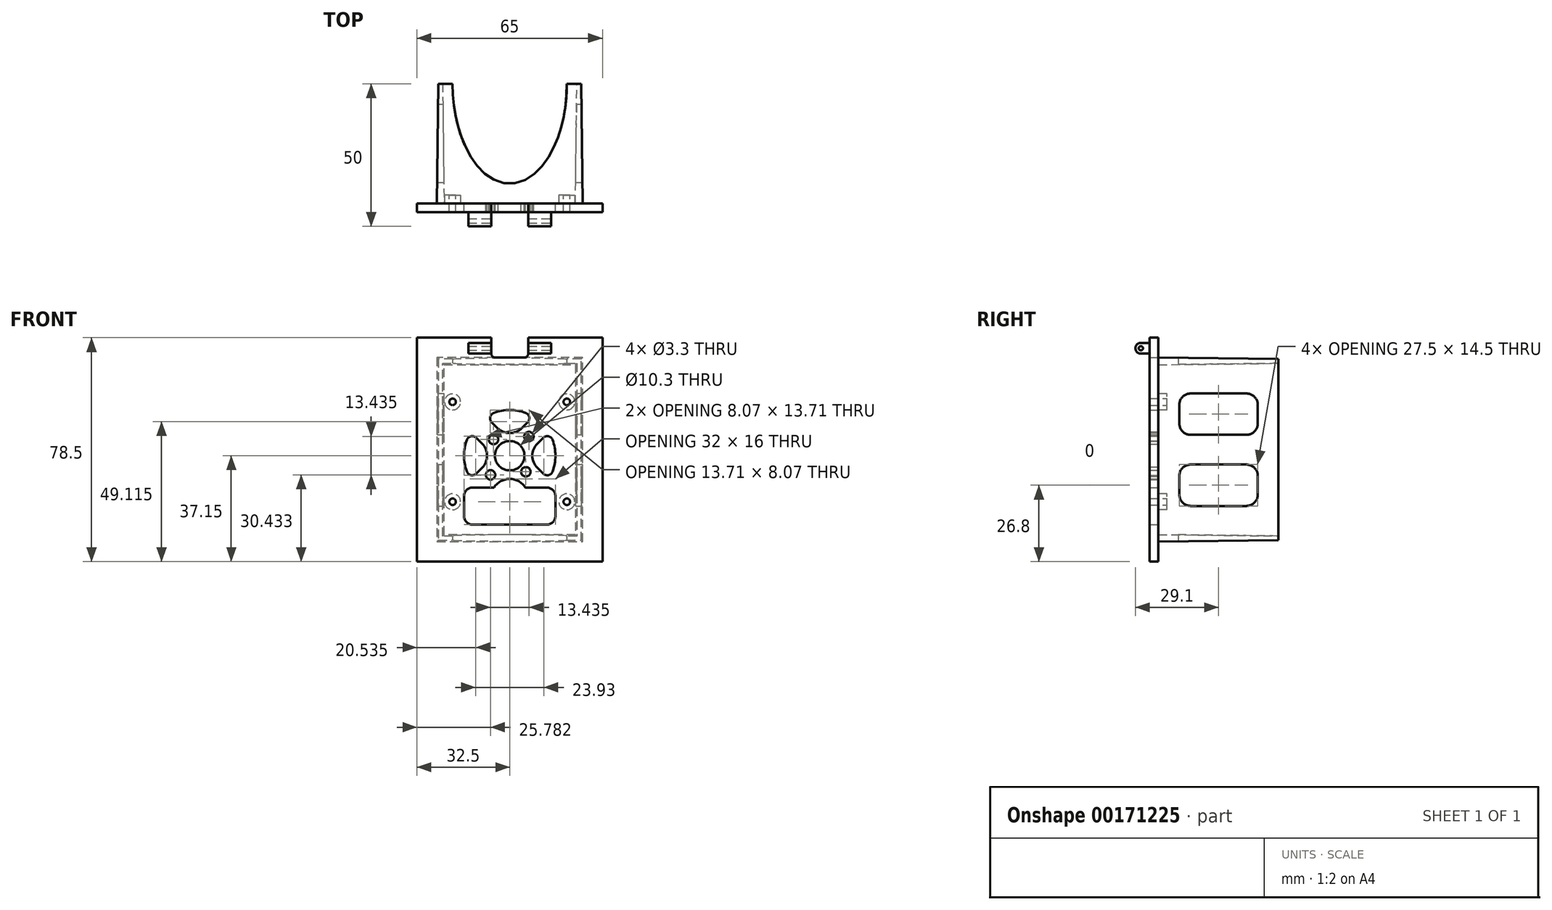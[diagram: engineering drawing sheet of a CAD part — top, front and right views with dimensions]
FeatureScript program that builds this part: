
annotation { "Feature Type Name" : "Feature", "Feature Type Description" : "" }
export const myFeature = defineFeature(function(context is Context, id is Id, definition is map)
    precondition{}
    {
        {
            var Q0;
            Q0=qCreatedBy(makeId("Front.planeOp"),FACE);
            var sketch = newSketch(context, id + "F0", { "sketchPlane" : qUnion([Q0])});
            skLineSegment(sketch, "E0.bottom", {"start": v(-32.5, 0) * mm, "end": v(32.5, 0) * mm});
            skLineSegment(sketch, "E0.top", {"start": v(-32.5, 78.5) * mm, "end": v(32.5, 78.5) * mm});
            skLineSegment(sketch, "E0.left", {"start": v(-32.5, 0) * mm, "end": v(-32.5, 78.5) * mm});
            skLineSegment(sketch, "E0.right", {"start": v(32.5, 0) * mm, "end": v(32.5, 78.5) * mm});
            skLineSegment(sketch, "E1", {"start": v(0, 0) * mm, "end": v(0, 78.5) * mm, "construction": true});
            skLineSegment(sketch, "E2", {"start": v(-6.5, 78.5) * mm, "end": v(-6.5, 73) * mm});
            skLineSegment(sketch, "E3", {"start": v(-5, 71.5) * mm, "end": v(0, 71.5) * mm});
            skLineSegment(sketch, "E4.MirrorCS", {"start": v(5, 71.5) * mm, "end": v(0, 71.5) * mm});
            skLineSegment(sketch, "E5.MirrorCS", {"start": v(6.5, 78.5) * mm, "end": v(6.5, 73) * mm});
            skPoint(sketch, "E6.visualSharp", {"position": v(-6.5, 71.5) * mm});
            skArc(sketch, "E6.filletArc", {"start": v(-6.5, 73) * mm, "mid": v(-6.06, 71.94) * mm, "end": v(-5, 71.5) * mm});
            skPoint(sketch, "E7.visualSharp", {"position": v(6.5, 71.5) * mm});
            skArc(sketch, "E7.filletArc", {"start": v(5, 71.5) * mm, "mid": v(6.06, 71.94) * mm, "end": v(6.5, 73) * mm});
            skCircle(sketch, "E8", {"center": v(0, 37.15) * mm, "radius": 5.15 * mm});
            skLineSegment(sketch, "E9.bottom", {"start": v(-13, 26) * mm, "end": v(-5.5, 26) * mm});
            skLineSegment(sketch, "E9.top", {"start": v(-13, 13) * mm, "end": v(13, 13) * mm});
            skLineSegment(sketch, "E9.left", {"start": v(-16, 23) * mm, "end": v(-16, 16) * mm});
            skLineSegment(sketch, "E9.right", {"start": v(16, 23) * mm, "end": v(16, 16) * mm});
            skPoint(sketch, "E9.middle", {"position": v(0, 19.5) * mm});
            skArc(sketch, "E10", {"start": v(5.5, 26) * mm, "mid": v(0, 29) * mm, "end": v(-5.5, 26) * mm});
            skLineSegment(sketch, "E11.trimOffspring", {"start": v(5.5, 26) * mm, "end": v(13, 26) * mm});
            skPoint(sketch, "E12.visualSharp", {"position": v(-16, 26) * mm});
            skArc(sketch, "E12.filletArc", {"start": v(-13, 26) * mm, "mid": v(-15.12, 25.12) * mm, "end": v(-16, 23) * mm});
            skPoint(sketch, "E13.visualSharp", {"position": v(-16, 13) * mm});
            skArc(sketch, "E13.filletArc", {"start": v(-16, 16) * mm, "mid": v(-15.12, 13.88) * mm, "end": v(-13, 13) * mm});
            skPoint(sketch, "E14.visualSharp", {"position": v(16, 13) * mm});
            skArc(sketch, "E14.filletArc", {"start": v(13, 13) * mm, "mid": v(15.12, 13.88) * mm, "end": v(16, 16) * mm});
            skPoint(sketch, "E15.visualSharp", {"position": v(16, 26) * mm});
            skArc(sketch, "E15.filletArc", {"start": v(16, 23) * mm, "mid": v(15.12, 25.12) * mm, "end": v(13, 26) * mm});
            skCircle(sketch, "E16", {"center": v(-20, 56) * mm, "radius": 1.15 * mm});
            skCircle(sketch, "E17", {"center": v(-20, 21) * mm, "radius": 1.15 * mm});
            skCircle(sketch, "E18.MirrorC", {"center": v(20, 56) * mm, "radius": 1.15 * mm});
            skCircle(sketch, "E19.MirrorC", {"center": v(20, 21) * mm, "radius": 1.15 * mm});
            skLineSegment(sketch, "E20", {"start": v(0, 37.15) * mm, "end": v(-11.31, 48.46) * mm, "construction": true});
            skLineSegment(sketch, "E21.1.0", {"start": v(0, 37.15) * mm, "end": v(-11.31, 25.84) * mm, "construction": true});
            skLineSegment(sketch, "E21.2.0", {"start": v(0, 37.15) * mm, "end": v(11.31, 25.84) * mm, "construction": true});
            skLineSegment(sketch, "E21.3.0", {"start": v(0, 37.15) * mm, "end": v(11.31, 48.46) * mm, "construction": true});
            skLineSegment(sketch, "E22", {"start": v(-4.24, 46.84) * mm, "end": v(-6.27, 48.87) * mm});
            skLineSegment(sketch, "E23.MirrorCS", {"start": v(4.24, 46.84) * mm, "end": v(6.27, 48.87) * mm});
            skArc(sketch, "E24", {"start": v(5.55, 52.16) * mm, "mid": v(0, 53.15) * mm, "end": v(-5.55, 52.16) * mm});
            skArc(sketch, "E25", {"start": v(-4.24, 46.84) * mm, "mid": v(0, 45.08) * mm, "end": v(4.24, 46.84) * mm});
            skPoint(sketch, "E26.orphan", {"position": v(2.24, 44.83) * mm});
            skPoint(sketch, "E27.orphan", {"position": v(-2.24, 44.83) * mm});
            skPoint(sketch, "E28.visualSharp", {"position": v(-8.26, 50.85) * mm});
            skArc(sketch, "E28.filletArc", {"start": v(-5.55, 52.16) * mm, "mid": v(-6.81, 50.7) * mm, "end": v(-6.27, 48.87) * mm});
            skPoint(sketch, "E29.visualSharp", {"position": v(8.26, 50.85) * mm});
            skArc(sketch, "E29.filletArc", {"start": v(6.27, 48.87) * mm, "mid": v(6.81, 50.7) * mm, "end": v(5.55, 52.16) * mm});
            skArc(sketch, "E30.MirrorCS", {"start": v(15, 42.7) * mm, "mid": v(16, 37.15) * mm, "end": v(15, 31.6) * mm});
            skArc(sketch, "E31.MirrorCS", {"start": v(11.72, 43.42) * mm, "mid": v(13.56, 43.96) * mm, "end": v(15, 42.7) * mm});
            skLineSegment(sketch, "E32.MirrorCS", {"start": v(9.69, 41.4) * mm, "end": v(11.72, 43.42) * mm});
            skArc(sketch, "E33.MirrorCS", {"start": v(9.69, 32.9) * mm, "mid": v(7.93, 37.15) * mm, "end": v(9.69, 41.4) * mm});
            skLineSegment(sketch, "E34.MirrorCS", {"start": v(9.69, 32.9) * mm, "end": v(11.72, 30.88) * mm});
            skArc(sketch, "E35.MirrorCS", {"start": v(15, 31.6) * mm, "mid": v(13.56, 30.34) * mm, "end": v(11.72, 30.88) * mm});
            skArc(sketch, "E36.MirrorCS", {"start": v(-15, 31.6) * mm, "mid": v(-16, 37.15) * mm, "end": v(-15, 42.7) * mm});
            skArc(sketch, "E37.MirrorCS", {"start": v(-11.72, 30.88) * mm, "mid": v(-13.56, 30.34) * mm, "end": v(-15, 31.6) * mm});
            skLineSegment(sketch, "E38.MirrorCS", {"start": v(-9.69, 32.9) * mm, "end": v(-11.72, 30.88) * mm});
            skArc(sketch, "E39.MirrorCS", {"start": v(-9.69, 41.4) * mm, "mid": v(-7.93, 37.15) * mm, "end": v(-9.69, 32.9) * mm});
            skLineSegment(sketch, "E40.MirrorCS", {"start": v(-9.69, 41.4) * mm, "end": v(-11.72, 43.42) * mm});
            skArc(sketch, "E41.MirrorCS", {"start": v(-15, 42.7) * mm, "mid": v(-13.56, 43.96) * mm, "end": v(-11.72, 43.42) * mm});
            skCircle(sketch, "E42", {"center": v(-5.66, 42.8) * mm, "radius": 1.65 * mm});
            skCircle(sketch, "E43.MirrorC", {"center": v(5.66, 31.5) * mm, "radius": 1.65 * mm});
            skCircle(sketch, "E44", {"center": v(-6.72, 30.43) * mm, "radius": 1.65 * mm});
            skCircle(sketch, "E45.MirrorC", {"center": v(6.72, 43.87) * mm, "radius": 1.65 * mm});
            skSolve(sketch);
        }
        {
            var Q0;
            Q0=makeQuery(id+"F0.imprint","IMPRINT",FACE,{"disambiguationData":[TD([[makeQuery(id+"F0.imprint","IMPRINT",EDGE,{"derivedFrom":sQuery(id+"F0.wireOp",EDGE,"E0.bottom")}),1.0]])]});
            extrude(context, id + "F1", {"entities" : qUnion([Q0]), "depth" : 3 * mm});
        }
        {
            var Q0;
            Q0=makeQuery(id+"F1.opExtrude","CAP_FACE",FACE,{"disambiguationData":[OSD([sQuery(id+"F0.wireOp",EDGE,"E0.bottom"),sQuery(id+"F0.wireOp",EDGE,"E0.top"),sQuery(id+"F0.wireOp",EDGE,"E0.left"),sQuery(id+"F0.wireOp",EDGE,"E0.right"),sQuery(id+"F0.wireOp",EDGE,"E2"),sQuery(id+"F0.wireOp",EDGE,"E3"),sQuery(id+"F0.wireOp",EDGE,"E4.MirrorCS"),sQuery(id+"F0.wireOp",EDGE,"E5.MirrorCS"),sQuery(id+"F0.wireOp",EDGE,"E6.filletArc"),sQuery(id+"F0.wireOp",EDGE,"E7.filletArc"),sQuery(id+"F0.wireOp",EDGE,"E8"),sQuery(id+"F0.wireOp",EDGE,"E9.bottom"),sQuery(id+"F0.wireOp",EDGE,"E9.top"),sQuery(id+"F0.wireOp",EDGE,"E9.left"),sQuery(id+"F0.wireOp",EDGE,"E9.right"),sQuery(id+"F0.wireOp",EDGE,"E10"),sQuery(id+"F0.wireOp",EDGE,"E11.trimOffspring"),sQuery(id+"F0.wireOp",EDGE,"E12.filletArc"),sQuery(id+"F0.wireOp",EDGE,"E13.filletArc"),sQuery(id+"F0.wireOp",EDGE,"E14.filletArc"),sQuery(id+"F0.wireOp",EDGE,"E15.filletArc"),sQuery(id+"F0.wireOp",EDGE,"E16"),sQuery(id+"F0.wireOp",EDGE,"E17"),sQuery(id+"F0.wireOp",EDGE,"E18.MirrorC"),sQuery(id+"F0.wireOp",EDGE,"E19.MirrorC"),sQuery(id+"F0.wireOp",EDGE,"E22"),sQuery(id+"F0.wireOp",EDGE,"E23.MirrorCS"),sQuery(id+"F0.wireOp",EDGE,"E24"),sQuery(id+"F0.wireOp",EDGE,"E25"),sQuery(id+"F0.wireOp",EDGE,"E28.filletArc"),sQuery(id+"F0.wireOp",EDGE,"E29.filletArc"),sQuery(id+"F0.wireOp",EDGE,"E30.MirrorCS"),sQuery(id+"F0.wireOp",EDGE,"E31.MirrorCS"),sQuery(id+"F0.wireOp",EDGE,"E32.MirrorCS"),sQuery(id+"F0.wireOp",EDGE,"E33.MirrorCS"),sQuery(id+"F0.wireOp",EDGE,"E34.MirrorCS"),sQuery(id+"F0.wireOp",EDGE,"E35.MirrorCS"),sQuery(id+"F0.wireOp",EDGE,"E36.MirrorCS"),sQuery(id+"F0.wireOp",EDGE,"E37.MirrorCS"),sQuery(id+"F0.wireOp",EDGE,"E38.MirrorCS"),sQuery(id+"F0.wireOp",EDGE,"E39.MirrorCS"),sQuery(id+"F0.wireOp",EDGE,"E40.MirrorCS"),sQuery(id+"F0.wireOp",EDGE,"E41.MirrorCS"),sQuery(id+"F0.wireOp",EDGE,"E42"),sQuery(id+"F0.wireOp",EDGE,"E43.MirrorC"),sQuery(id+"F0.wireOp",EDGE,"E44"),sQuery(id+"F0.wireOp",EDGE,"E45.MirrorC")])],"isStart":true});
            var sketch = newSketch(context, id + "F2", { "sketchPlane" : qUnion([Q0])});
            skLineSegment(sketch, "E46.bottom", {"start": v(-25.5, 71.5) * mm, "end": v(25.5, 71.5) * mm});
            skLineSegment(sketch, "E46.top", {"start": v(-25.5, 7) * mm, "end": v(25.5, 7) * mm});
            skLineSegment(sketch, "E46.left", {"start": v(-25.5, 71.5) * mm, "end": v(-25.5, 7) * mm});
            skLineSegment(sketch, "E46.right", {"start": v(25.5, 71.5) * mm, "end": v(25.5, 7) * mm});
            skLineSegment(sketch, "E47.0", {"start": v(-23, 69) * mm, "end": v(23, 69) * mm});
            skLineSegment(sketch, "E47.1", {"start": v(-23, 69) * mm, "end": v(-23, 9.5) * mm});
            skLineSegment(sketch, "E47.2", {"start": v(-23, 9.5) * mm, "end": v(23, 9.5) * mm});
            skLineSegment(sketch, "E47.3", {"start": v(23, 69) * mm, "end": v(23, 9.5) * mm});
            skLineSegment(sketch, "E48.0", {"start": v(-37.5, -5) * mm, "end": v(37.5, -5) * mm});
            skLineSegment(sketch, "E48.1", {"start": v(-37.5, 83.5) * mm, "end": v(-37.5, -5) * mm});
            skLineSegment(sketch, "E48.2", {"start": v(37.5, -5) * mm, "end": v(37.5, 83.5) * mm});
            skLineSegment(sketch, "E48.3", {"start": v(-1.5, 83.5) * mm, "end": v(-37.5, 83.5) * mm});
            skLineSegment(sketch, "E48.4", {"start": v(37.5, 83.5) * mm, "end": v(1.5, 83.5) * mm});
            skLineSegment(sketch, "E48.5", {"start": v(1.5, 83.5) * mm, "end": v(1.5, 76.5) * mm});
            skLineSegment(sketch, "E48.6", {"start": v(1.5, 76.5) * mm, "end": v(-1.5, 76.5) * mm});
            skLineSegment(sketch, "E48.7", {"start": v(-1.5, 76.5) * mm, "end": v(-1.5, 83.5) * mm});
            skCircle(sketch, "E49", {"center": v(-20, 56) * mm, "radius": 2.8 * mm});
            skCircle(sketch, "E50", {"center": v(20, 56) * mm, "radius": 2.8 * mm});
            skCircle(sketch, "E51", {"center": v(20, 21) * mm, "radius": 2.8 * mm});
            skCircle(sketch, "E52", {"center": v(-20, 21) * mm, "radius": 2.8 * mm});
            skSolve(sketch);
        }
        {
            var Q0;
            Q0=makeQuery(id+"F2.imprint","IMPRINT",FACE,{"disambiguationData":[TD([[makeQuery(id+"F2.imprint","IMPRINT",EDGE,{"derivedFrom":sQuery(id+"F2.wireOp",EDGE,"E46.top")}),1.0]])]});
            extrude(context, id + "F3", {"entities" : qUnion([Q0]), "operationType" : NewBodyOperationType.ADD, "depth" : 42 * mm, "hasDraft" : true, "draftAngle" : .67 * degree, "draftPullDirection" : true});
        }
        {
            var Q0;
            Q0=makeQuery(id+"F2.imprint","IMPRINT",FACE,{"disambiguationData":[TD([[makeQuery(id+"F2.imprint","IMPRINT",EDGE,{"derivedFrom":sQuery(id+"F2.wireOp",EDGE,"E49")}),1.0]])]});
            var Q1;
            Q1=makeQuery(id+"F2.imprint","IMPRINT",FACE,{"disambiguationData":[TD([[makeQuery(id+"F2.imprint","IMPRINT",EDGE,{"derivedFrom":sQuery(id+"F2.wireOp",EDGE,"E50")}),1.0]])]});
            var Q2;
            Q2=makeQuery(id+"F2.imprint","IMPRINT",FACE,{"disambiguationData":[TD([[makeQuery(id+"F2.imprint","IMPRINT",EDGE,{"derivedFrom":sQuery(id+"F2.wireOp",EDGE,"E51")}),1.0]])]});
            var Q3;
            Q3=makeQuery(id+"F2.imprint","IMPRINT",FACE,{"disambiguationData":[TD([[makeQuery(id+"F2.imprint","IMPRINT",EDGE,{"derivedFrom":sQuery(id+"F2.wireOp",EDGE,"E52")}),1.0]])]});
            extrude(context, id + "F4", {"entities" : qUnion([Q0, Q1, Q2, Q3]), "operationType" : NewBodyOperationType.ADD, "depth" : 3 * mm});
        }
        {
            var Q0;
            Q0=qCreatedBy(makeId("Top.planeOp"),FACE);
            var sketch = newSketch(context, id + "F5", { "sketchPlane" : qUnion([Q0])});
            skEllipse(sketch, "E53", {"center": v(0, 42) * mm, "majorRadius": 20 * mm, "minorRadius": 35 * mm, "majorAxis": v(1, 0)});
            skSolve(sketch);
        }
        {
            var Q0;
            Q0=makeQuery(id+"F5.imprint","IMPRINT",FACE,{"disambiguationData":[TD([[makeQuery(id+"F5.imprint","IMPRINT",EDGE,{"derivedFrom":sQuery(id+"F5.wireOp",EDGE,"E53")}),1.0]])]});
            var Q1;
            Q1=makeQuery(id+"F3.opExtrude","SWEPT_FACE",FACE,{"disambiguationData":[OSD([sQuery(id+"F2.wireOp",EDGE,"E46.bottom")])]});
            extrude(context, id + "F6", {"entities" : qUnion([Q0]), "operationType" : NewBodyOperationType.REMOVE, "endBound" : BoundingType.UP_TO_SURFACE, "endBoundEntityFace" : qUnion([Q1]), "depth" : 25 * mm});
        }
        {
            var Q0;
            Q0=qCreatedBy(makeId("Right.planeOp"),FACE);
            var sketch = newSketch(context, id + "F7", { "sketchPlane" : qUnion([Q0])});
            skLineSegment(sketch, "E54.bottom", {"start": v(30.85, 58.95) * mm, "end": v(11.35, 58.95) * mm});
            skLineSegment(sketch, "E54.top", {"start": v(30.85, 44.45) * mm, "end": v(11.35, 44.45) * mm});
            skLineSegment(sketch, "E54.left", {"start": v(34.85, 54.95) * mm, "end": v(34.85, 48.45) * mm});
            skLineSegment(sketch, "E54.right", {"start": v(7.35, 54.95) * mm, "end": v(7.35, 48.45) * mm});
            skPoint(sketch, "E55.visualSharp", {"position": v(34.85, 58.95) * mm});
            skArc(sketch, "E55.filletArc", {"start": v(34.85, 54.95) * mm, "mid": v(33.68, 57.78) * mm, "end": v(30.85, 58.95) * mm});
            skPoint(sketch, "E56.visualSharp", {"position": v(7.35, 58.95) * mm});
            skArc(sketch, "E56.filletArc", {"start": v(11.35, 58.95) * mm, "mid": v(8.52, 57.78) * mm, "end": v(7.35, 54.95) * mm});
            skPoint(sketch, "E57.visualSharp", {"position": v(7.35, 44.45) * mm});
            skArc(sketch, "E57.filletArc", {"start": v(7.35, 48.45) * mm, "mid": v(8.52, 45.62) * mm, "end": v(11.35, 44.45) * mm});
            skPoint(sketch, "E58.visualSharp", {"position": v(34.85, 44.45) * mm});
            skArc(sketch, "E58.filletArc", {"start": v(30.85, 44.45) * mm, "mid": v(33.68, 45.62) * mm, "end": v(34.85, 48.45) * mm});
            skLineSegment(sketch, "E59.0.0", {"start": v(0, 7) * mm, "end": v(0, 71.5) * mm, "construction": true});
            skLineSegment(sketch, "E59.0.1", {"start": v(0, 71.5) * mm, "end": v(42, 71) * mm, "construction": true});
            skLineSegment(sketch, "E59.0.2", {"start": v(42, 71) * mm, "end": v(42, 7.5) * mm, "construction": true});
            skLineSegment(sketch, "E59.0.3", {"start": v(42, 7.5) * mm, "end": v(0, 7) * mm, "construction": true});
            skLineSegment(sketch, "E60", {"start": v(0, 39.25) * mm, "end": v(42, 39.25) * mm, "construction": true});
            skArc(sketch, "E61.MirrorCS", {"start": v(7.35, 30.05) * mm, "mid": v(8.52, 32.88) * mm, "end": v(11.35, 34.05) * mm});
            skArc(sketch, "E62.MirrorCS", {"start": v(30.85, 34.05) * mm, "mid": v(33.68, 32.88) * mm, "end": v(34.85, 30.05) * mm});
            skArc(sketch, "E63.MirrorCS", {"start": v(11.35, 19.55) * mm, "mid": v(8.52, 20.72) * mm, "end": v(7.35, 23.55) * mm});
            skArc(sketch, "E64.MirrorCS", {"start": v(34.85, 23.55) * mm, "mid": v(33.68, 20.72) * mm, "end": v(30.85, 19.55) * mm});
            skPoint(sketch, "E65.MirrorP", {"position": v(7.35, 34.05) * mm});
            skLineSegment(sketch, "E66.MirrorCS", {"start": v(30.85, 34.05) * mm, "end": v(11.35, 34.05) * mm});
            skPoint(sketch, "E67.MirrorP", {"position": v(34.85, 19.55) * mm});
            skLineSegment(sketch, "E68.MirrorCS", {"start": v(34.85, 23.55) * mm, "end": v(34.85, 30.05) * mm});
            skLineSegment(sketch, "E69.MirrorCS", {"start": v(30.85, 19.55) * mm, "end": v(11.35, 19.55) * mm});
            skLineSegment(sketch, "E70.MirrorCS", {"start": v(7.35, 23.55) * mm, "end": v(7.35, 30.05) * mm});
            skPoint(sketch, "E71.MirrorP", {"position": v(34.85, 34.05) * mm});
            skPoint(sketch, "E72.MirrorP", {"position": v(7.35, 19.55) * mm});
            skSolve(sketch);
        }
        {
            var Q0;
            Q0 = qSketchRegion(id + "F7", true);
            var Q1;
            Q1=makeQuery(id+"F3.opExtrude","SWEPT_FACE",FACE,{"disambiguationData":[OSD([sQuery(id+"F2.wireOp",EDGE,"E46.right")])]});
            var Q2;
            Q2=makeQuery(id+"F3.opExtrude","SWEPT_FACE",FACE,{"disambiguationData":[OSD([sQuery(id+"F2.wireOp",EDGE,"E46.left")])]});
            extrude(context, id + "F8", {"entities" : qUnion([Q0]), "operationType" : NewBodyOperationType.REMOVE, "endBound" : BoundingType.UP_TO_SURFACE, "oppositeDirection" : true, "endBoundEntityFace" : qUnion([Q1]), "depth" : 50 * mm, "hasSecondDirection" : true, "secondDirectionBound" : SecondDirectionBoundingType.UP_TO_SURFACE, "secondDirectionOppositeDirection" : false, "secondDirectionBoundEntityFace" : qUnion([Q2]), "secondDirectionDepth" : 25 * mm});
        }
        {
            var Q0;
            Q0=makeQuery(id+"F1.opExtrude","CAP_FACE",FACE,{"disambiguationData":[OSD([sQuery(id+"F0.wireOp",EDGE,"E0.bottom"),sQuery(id+"F0.wireOp",EDGE,"E0.top"),sQuery(id+"F0.wireOp",EDGE,"E0.left"),sQuery(id+"F0.wireOp",EDGE,"E0.right"),sQuery(id+"F0.wireOp",EDGE,"E2"),sQuery(id+"F0.wireOp",EDGE,"E3"),sQuery(id+"F0.wireOp",EDGE,"E4.MirrorCS"),sQuery(id+"F0.wireOp",EDGE,"E5.MirrorCS"),sQuery(id+"F0.wireOp",EDGE,"E6.filletArc"),sQuery(id+"F0.wireOp",EDGE,"E7.filletArc"),sQuery(id+"F0.wireOp",EDGE,"E8"),sQuery(id+"F0.wireOp",EDGE,"E9.bottom"),sQuery(id+"F0.wireOp",EDGE,"E9.top"),sQuery(id+"F0.wireOp",EDGE,"E9.left"),sQuery(id+"F0.wireOp",EDGE,"E9.right"),sQuery(id+"F0.wireOp",EDGE,"E10"),sQuery(id+"F0.wireOp",EDGE,"E11.trimOffspring"),sQuery(id+"F0.wireOp",EDGE,"E12.filletArc"),sQuery(id+"F0.wireOp",EDGE,"E13.filletArc"),sQuery(id+"F0.wireOp",EDGE,"E14.filletArc"),sQuery(id+"F0.wireOp",EDGE,"E15.filletArc"),sQuery(id+"F0.wireOp",EDGE,"E16"),sQuery(id+"F0.wireOp",EDGE,"E17"),sQuery(id+"F0.wireOp",EDGE,"E18.MirrorC"),sQuery(id+"F0.wireOp",EDGE,"E19.MirrorC"),sQuery(id+"F0.wireOp",EDGE,"E22"),sQuery(id+"F0.wireOp",EDGE,"E23.MirrorCS"),sQuery(id+"F0.wireOp",EDGE,"E24"),sQuery(id+"F0.wireOp",EDGE,"E25"),sQuery(id+"F0.wireOp",EDGE,"E28.filletArc"),sQuery(id+"F0.wireOp",EDGE,"E29.filletArc"),sQuery(id+"F0.wireOp",EDGE,"E30.MirrorCS"),sQuery(id+"F0.wireOp",EDGE,"E31.MirrorCS"),sQuery(id+"F0.wireOp",EDGE,"E32.MirrorCS"),sQuery(id+"F0.wireOp",EDGE,"E33.MirrorCS"),sQuery(id+"F0.wireOp",EDGE,"E34.MirrorCS"),sQuery(id+"F0.wireOp",EDGE,"E35.MirrorCS"),sQuery(id+"F0.wireOp",EDGE,"E36.MirrorCS"),sQuery(id+"F0.wireOp",EDGE,"E37.MirrorCS"),sQuery(id+"F0.wireOp",EDGE,"E38.MirrorCS"),sQuery(id+"F0.wireOp",EDGE,"E39.MirrorCS"),sQuery(id+"F0.wireOp",EDGE,"E40.MirrorCS"),sQuery(id+"F0.wireOp",EDGE,"E41.MirrorCS"),sQuery(id+"F0.wireOp",EDGE,"E42"),sQuery(id+"F0.wireOp",EDGE,"E43.MirrorC"),sQuery(id+"F0.wireOp",EDGE,"E44"),sQuery(id+"F0.wireOp",EDGE,"E45.MirrorC")])],"isStart":false});
            var sketch = newSketch(context, id + "F9", { "sketchPlane" : qUnion([Q0])});
            skLineSegment(sketch, "E73.bottom", {"start": v(-14.5, 76.7) * mm, "end": v(-6.5, 76.7) * mm});
            skLineSegment(sketch, "E73.top", {"start": v(-14.5, 72.9) * mm, "end": v(-6.5, 72.9) * mm});
            skLineSegment(sketch, "E73.left", {"start": v(-14.5, 76.7) * mm, "end": v(-14.5, 72.9) * mm});
            skLineSegment(sketch, "E73.right", {"start": v(-6.5, 76.7) * mm, "end": v(-6.5, 72.9) * mm});
            skLineSegment(sketch, "E74", {"start": v(0, 71.5) * mm, "end": v(0, 83.16) * mm, "construction": true});
            skPoint(sketch, "E74.endSnap0", {"position": v(0, 71.5) * mm});
            skLineSegment(sketch, "E75.MirrorCS", {"start": v(6.5, 76.7) * mm, "end": v(6.5, 72.9) * mm});
            skLineSegment(sketch, "E76.MirrorCS", {"start": v(14.5, 72.9) * mm, "end": v(6.5, 72.9) * mm});
            skLineSegment(sketch, "E77.MirrorCS", {"start": v(14.5, 76.7) * mm, "end": v(6.5, 76.7) * mm});
            skLineSegment(sketch, "E78.MirrorCS", {"start": v(14.5, 76.7) * mm, "end": v(14.5, 72.9) * mm});
            skSolve(sketch);
        }
        {
            var Q0;
            {var subQ2=sQuery(id+"F9.wireOp",EDGE,"E73.bottom");Q0=makeQuery(id+"F9.imprint","IMPRINT",FACE,{"disambiguationData":[TD([[makeQuery(id+"F9.imprint","IMPRINT",EDGE,{"derivedFrom":subQ2}),-1.0]])]});}
            var Q1;
            {var subQ1=sQuery(id+"F9.wireOp",EDGE,"E76.MirrorCS");Q1=makeQuery(id+"F9.imprint","IMPRINT",FACE,{"disambiguationData":[TD([[makeQuery(id+"F9.imprint","IMPRINT",EDGE,{"derivedFrom":subQ1}),-1.0]])]});}
            extrude(context, id + "F10", {"entities" : qUnion([Q0, Q1]), "operationType" : NewBodyOperationType.ADD, "depth" : 5 * mm});
        }
        {
            var Q0;
            Q0=makeQuery(id+"F10.opExtrude","CAP_EDGE",EDGE,{"disambiguationData":[OSD([sQuery(id+"F9.wireOp",EDGE,"E73.top")])],"isStart":false});
            var Q1;
            Q1=makeQuery(id+"F10.opExtrude","CAP_EDGE",EDGE,{"disambiguationData":[OSD([sQuery(id+"F9.wireOp",EDGE,"E73.bottom")])],"isStart":false});
            var Q2;
            Q2=makeQuery(id+"F10.opExtrude","CAP_EDGE",EDGE,{"disambiguationData":[OSD([sQuery(id+"F9.wireOp",EDGE,"E77.MirrorCS")])],"isStart":false});
            var Q3;
            Q3=makeQuery(id+"F10.opExtrude","CAP_EDGE",EDGE,{"disambiguationData":[OSD([sQuery(id+"F9.wireOp",EDGE,"E76.MirrorCS")])],"isStart":false});
            fillet(context, id + "F11", {"entities" : qUnion([Q0, Q1, Q2, Q3]), "radius" : (3.8 / 2) * mm, "tangentPropagation" : true, "allowEdgeOverflow" : false});
        }
        {
            var Q0;
            Q0=makeQuery(id+"F10.boolean.opBoolean","MERGE",FACE,{"derivedFrom":[makeQuery(id+"F1.opExtrude","SWEPT_FACE",FACE,{"disambiguationData":[OSD([sQuery(id+"F0.wireOp",EDGE,"E2")])]}),makeQuery(id+"F10.opExtrude","SWEPT_FACE",FACE,{"disambiguationData":[OSD([sQuery(id+"F9.wireOp",EDGE,"E73.right")])]})]});
            var sketch = newSketch(context, id + "F12", { "sketchPlane" : qUnion([Q0])});
            skCircle(sketch, "E79", {"center": v(-6.1, 74.8) * mm, "radius": 0.75 * mm});
            skSolve(sketch);
        }
        {
            var Q0;
            Q0 = qSketchRegion(id + "F12", true);
            extrude(context, id + "F13", {"entities" : qUnion([Q0]), "operationType" : NewBodyOperationType.REMOVE, "oppositeDirection" : true, "depth" : 25 * mm, "hasSecondDirection" : true, "secondDirectionOppositeDirection" : false, "secondDirectionDepth" : 25 * mm});
        }
    });
